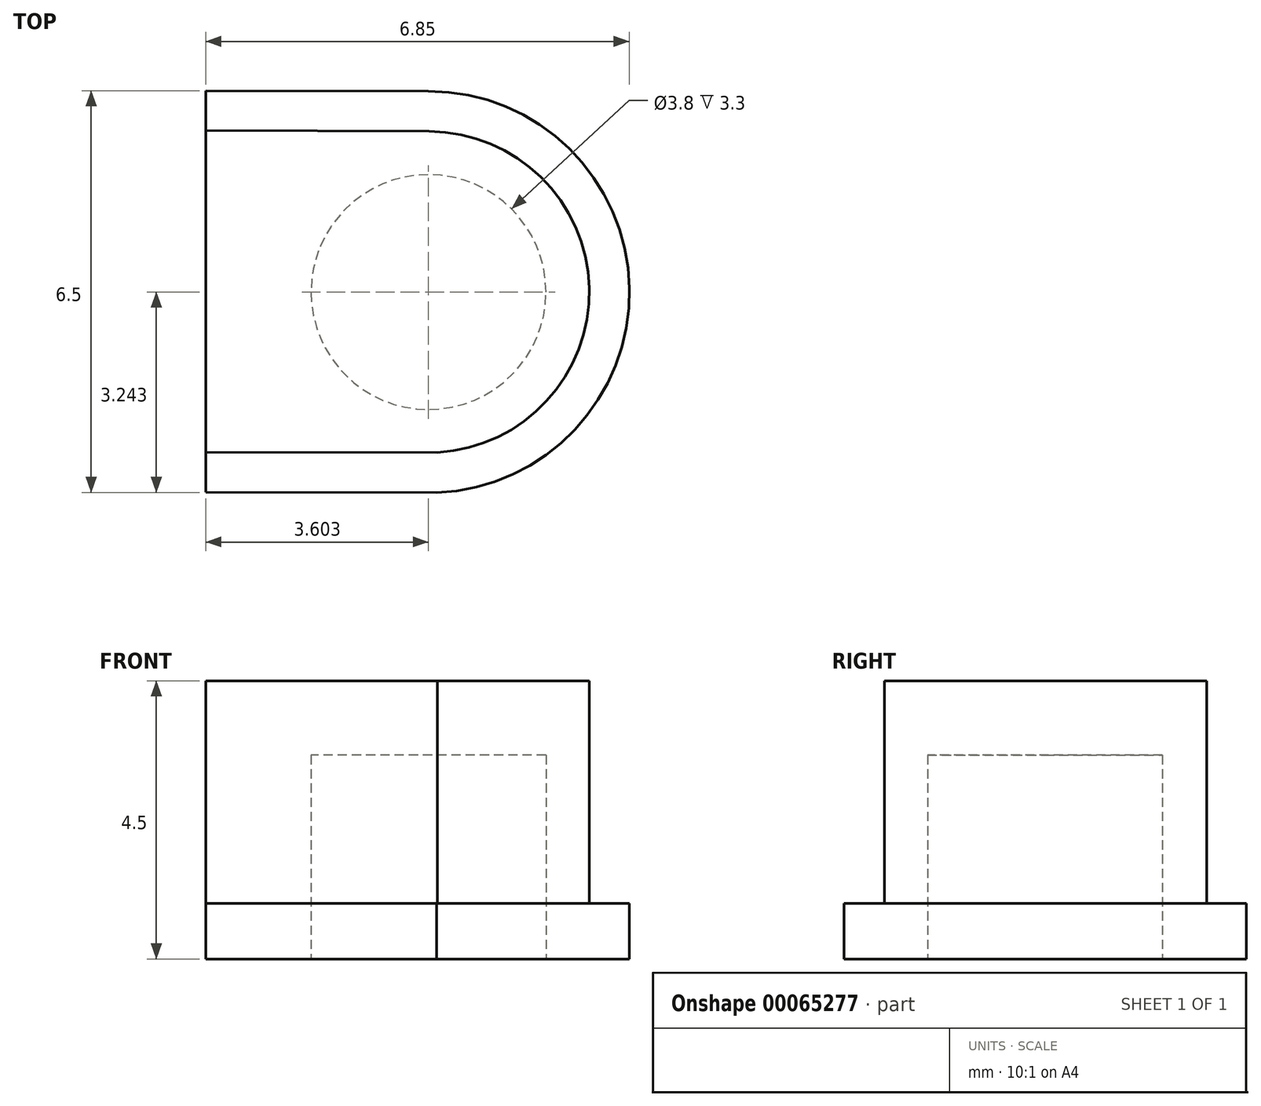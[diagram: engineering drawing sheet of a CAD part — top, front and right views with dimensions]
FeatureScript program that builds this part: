
annotation { "Feature Type Name" : "Feature", "Feature Type Description" : "" }
export const myFeature = defineFeature(function(context is Context, id is Id, definition is map)
    precondition{}
    {
        {
            var Q0;
            Q0=qCreatedBy(makeId("Top.planeOp"),FACE);
            var sketch = newSketch(context, id + "F0", { "sketchPlane" : qUnion([Q0])});
            skLineSegment(sketch, "E0", {"start": v(0, 0) * mm, "end": v(-3.9, 0) * mm, "construction": true});
            skArc(sketch, "E1", {"start": v(-3.9, 2.6) * mm, "mid": v(-6.5, -0.06) * mm, "end": v(-3.77, -2.6) * mm});
            skLineSegment(sketch, "E2", {"start": v(-3.9, 2.6) * mm, "end": v(-0.3, 2.6) * mm});
            skCircle(sketch, "E3", {"center": v(-3.9, 0) * mm, "radius": 1.9 * mm});
            skCircle(sketch, "E4", {"center": v(3.9, -0.02) * mm, "radius": 1.9 * mm});
            skArc(sketch, "E5", {"start": v(-3.9, 3.25) * mm, "mid": v(-7.15, 0) * mm, "end": v(-3.9, -3.25) * mm});
            skArc(sketch, "E6", {"start": v(4.03, -3.26) * mm, "mid": v(7.15, 0.05) * mm, "end": v(3.9, 3.23) * mm});
            skLineSegment(sketch, "E7", {"start": v(3.9, 3.23) * mm, "end": v(0.3, 3.24) * mm});
            skLineSegment(sketch, "E8", {"start": v(4.03, -3.26) * mm, "end": v(-3.9, -3.25) * mm});
            skLineSegment(sketch, "E9.rect.bottom", {"start": v(0.3, -3.26) * mm, "end": v(-0.3, -3.26) * mm});
            skLineSegment(sketch, "E9.rect.left", {"start": v(0.3, -3.26) * mm, "end": v(0.3, 3.24) * mm});
            skLineSegment(sketch, "E9.rect.right", {"start": v(-0.3, -3.26) * mm, "end": v(-0.3, 3.26) * mm});
            skPoint(sketch, "E9.rect.middle", {"position": v(0, 0) * mm});
            skLineSegment(sketch, "E10.trimOffspring", {"start": v(-0.3, 3.24) * mm, "end": v(-3.9, 3.25) * mm});
            skPoint(sketch, "E11.orphan", {"position": v(0.3, 3.26) * mm});
            skArc(sketch, "E12", {"start": v(4.05, -2.61) * mm, "mid": v(6.5, 0.05) * mm, "end": v(3.91, 2.58) * mm});
            skLineSegment(sketch, "E13", {"start": v(4.05, -2.61) * mm, "end": v(0.3, -2.6) * mm});
            skLineSegment(sketch, "E14", {"start": v(0.3, 2.6) * mm, "end": v(3.91, 2.58) * mm});
            skLineSegment(sketch, "E15.trimOffspring", {"start": v(-0.3, -2.6) * mm, "end": v(-3.78, -2.6) * mm});
            skPoint(sketch, "E16.orphan", {"position": v(-3.9, -2.6) * mm});
            skSolve(sketch);
        }
        {
            var Q0;
            {var subQ1=sQuery(id+"F0.wireOp",EDGE,"E2");Q0=makeQuery(id+"F0.imprint","IMPRINT",FACE,{"disambiguationData":[TD([[makeQuery(id+"F0.imprint","IMPRINT",EDGE,{"derivedFrom":subQ1}),-1.0]])]});}
            var Q1;
            Q1=makeQuery(id+"F0.imprint","IMPRINT",FACE,{"disambiguationData":[TD([[makeQuery(id+"F0.imprint","IMPRINT",EDGE,{"derivedFrom":sQuery(id+"F0.wireOp",EDGE,"E4")}),-1.0]])]});
            var Q2;
            {var subQ4=sQuery(id+"F0.wireOp",EDGE,"E6");Q2=makeQuery(id+"F0.imprint","IMPRINT",FACE,{"disambiguationData":[TD([[makeQuery(id+"F0.imprint","IMPRINT",EDGE,{"derivedFrom":subQ4}),1.0]])]});}
            var Q3;
            {var subQ5=sQuery(id+"F0.wireOp",EDGE,"E2");Q3=makeQuery(id+"F0.imprint","IMPRINT",FACE,{"disambiguationData":[TD([[makeQuery(id+"F0.imprint","IMPRINT",EDGE,{"derivedFrom":subQ5}),1.0]])]});}
            var Q4;
            Q4=makeQuery(id+"F0.imprint","IMPRINT",FACE,{"disambiguationData":[TD([[makeQuery(id+"F0.imprint","IMPRINT",EDGE,{"derivedFrom":sQuery(id+"F0.wireOp",EDGE,"E3")}),1.0]])]});
            var Q5;
            Q5=makeQuery(id+"F0.imprint","IMPRINT",FACE,{"disambiguationData":[TD([[makeQuery(id+"F0.imprint","IMPRINT",EDGE,{"derivedFrom":sQuery(id+"F0.wireOp",EDGE,"E4")}),1.0]])]});
            extrude(context, id + "F1", {"entities" : qUnion([Q0, Q1, Q2, Q3, Q4, Q5]), "depth" : 0.9 * mm});
        }
        {
            var Q0;
            {var subQ1=sQuery(id+"F0.wireOp",EDGE,"E2");Q0=makeQuery(id+"F0.imprint","IMPRINT",FACE,{"disambiguationData":[TD([[makeQuery(id+"F0.imprint","IMPRINT",EDGE,{"derivedFrom":subQ1}),-1.0]])]});}
            var Q1;
            Q1=makeQuery(id+"F0.imprint","IMPRINT",FACE,{"disambiguationData":[TD([[makeQuery(id+"F0.imprint","IMPRINT",EDGE,{"derivedFrom":sQuery(id+"F0.wireOp",EDGE,"E4")}),-1.0]])]});
            var Q2;
            Q2=makeQuery(id+"F0.imprint","IMPRINT",FACE,{"disambiguationData":[TD([[makeQuery(id+"F0.imprint","IMPRINT",EDGE,{"derivedFrom":sQuery(id+"F0.wireOp",EDGE,"E3")}),1.0]])]});
            var Q3;
            Q3=makeQuery(id+"F0.imprint","IMPRINT",FACE,{"disambiguationData":[TD([[makeQuery(id+"F0.imprint","IMPRINT",EDGE,{"derivedFrom":sQuery(id+"F0.wireOp",EDGE,"E4")}),1.0]])]});
            extrude(context, id + "F2", {"entities" : qUnion([Q0, Q1, Q2, Q3]), "operationType" : NewBodyOperationType.ADD, "depth" : 4.5 * mm});
        }
        {
            var Q0;
            Q0=makeQuery(id+"F0.imprint","IMPRINT",FACE,{"disambiguationData":[TD([[makeQuery(id+"F0.imprint","IMPRINT",EDGE,{"derivedFrom":sQuery(id+"F0.wireOp",EDGE,"E3")}),1.0]])]});
            var Q1;
            Q1=makeQuery(id+"F0.imprint","IMPRINT",FACE,{"disambiguationData":[TD([[makeQuery(id+"F0.imprint","IMPRINT",EDGE,{"derivedFrom":sQuery(id+"F0.wireOp",EDGE,"E4")}),1.0]])]});
            extrude(context, id + "F3", {"entities" : qUnion([Q0, Q1]), "operationType" : NewBodyOperationType.REMOVE, "depth" : 3.3 * mm});
        }
        {
            var Q0;
            Q0=makeQuery(id+"F1.opExtrude","SWEPT_BODY",BODY,{"disambiguationData":[OSD([sQuery(id+"F0.wireOp",EDGE,"E5"),sQuery(id+"F0.wireOp",EDGE,"E8"),sQuery(id+"F0.wireOp",EDGE,"E9.rect.right"),sQuery(id+"F0.wireOp",EDGE,"E10.trimOffspring")])]});
            deleteBodies(context, id + "F4", {"entities" : qUnion([Q0])});
        }
    });
